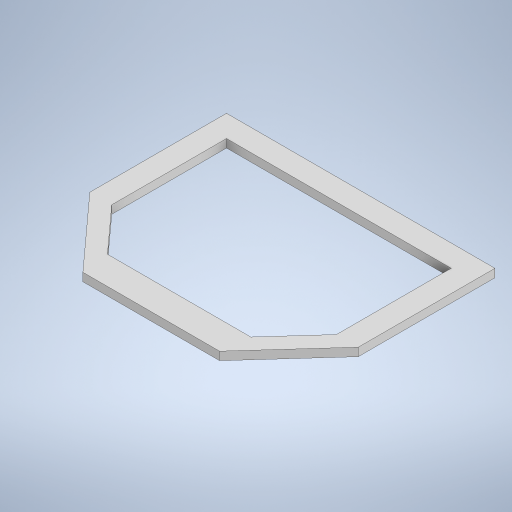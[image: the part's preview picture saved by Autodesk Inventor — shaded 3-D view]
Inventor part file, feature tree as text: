
AUTODESK INVENTOR PART (.ipt)
format: ipt  version: 2024.2 (Build 282272000, 272)  size: 262,656 bytes
history: native  units: mm
features: extrude x1, sketch x1
ambient origin geometry x8: Origin, YZ Plane, XZ Plane, XY Plane, X Axis, Y Axis, Z Axis, Center Point
bodies: Solid1 (feature_tree)
feature tree (2):
  extrude  "Extrusion1"  Depth=50.0mm
  sketch  "Sketch1"  dims[d0=98.2mm d1=50.0mm d2=50.0mm d5=26.635mm d6=24.1mm d7=24.1mm d9=8.0mm d10=8.0mm d11=42.0mm d12=3.0mm d13=0.0mm]
